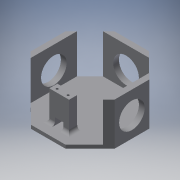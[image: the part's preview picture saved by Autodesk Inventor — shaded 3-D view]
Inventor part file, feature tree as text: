
AUTODESK INVENTOR PART (.ipt)
format: ipt  version: 2017 (Build 210142000, 142)  size: 202,752 bytes
history: native  units: in
note: dims shown in document units (in); Inventor stores cm internally (conversion verified against a paired STEP export)
features: reference x10, extrude x9, sketch x9, other x6, fillet x1
ambient origin geometry x8: Origin, YZ Plane, XZ Plane, XY Plane, X Axis, Y Axis, Z Axis, Center Point
bodies: Solid1 (feature_tree)
feature tree (35):
  extrude  "Extrusion1"  Depth=0.125in TaperAngle=0.0deg
  extrude  "Extrusion2"  Depth=0.205in
  extrude  "Extrusion3"  Depth=1.4in
  extrude  "Extrusion4"  Depth=0.01in
  extrude  "Extrusion5"  Depth=0.205in
  extrude  "Extrusion6"  Depth=1.4in
  extrude  "Extrusion7"  Depth=1.05in TaperAngle=0.0deg
  extrude  "Extrusion8"  Depth=0.08in
  extrude  "Extrusion9"  Depth=0.5in TaperAngle=0.0deg
  fillet  "Fillet2"  Radius=0.2045in
  sketch  "Sketch1"  dims[d0=3.0in d1=0.125in d2=0.0in]
  sketch  "Sketch3"  dims[d5=0.205in d6=0.205in]
  sketch  "Sketch5"  dims[d7=1.4in d8=0.0in d9=0.01in]
  reference  "Reference1"
  sketch  "Sketch6"  dims[d10=1.04in d11=0.0in d12=0.01in]
  reference  "Reference2"
  sketch  "Sketch7"  dims[d13=1.04in d14=0.0in d15=0.205in]
  sketch  "Sketch8"  dims[d16=1.4in d17=0.0in d18=0.01in]
  reference  "Reference3"
  sketch  "Sketch9"  dims[d19=1.04in d20=0.0in d21=1.05in d22=0.0in]
  reference  "Reference4"
  reference  "Reference5"
  reference  "Reference6"
  sketch  "Sketch10"  dims[d24=0.0531in d25=0.08in]
  reference  "Reference7"
  reference  "Reference8"
  reference  "Reference9"
  reference  "Reference10"
  sketch  "Sketch11"  dims[d26=0.08in d27=0.5in d28=0.0in d31=0.2045in d32=0.3in d33=0.25in d34=0.5in d35=0.0in d36=0.0in d37=0.125in]
  parser-record x1  (decoder bookkeeping rows leaked as tree rows — omitted from the tree; the rows remain in map.json)
  other  "Main_Assy.iam"
  other  "PIR_Sensor:1"
  other  "PIR_Sensor:3"
  other  "PIR_Sensor:2"
  other  "Servo Futaba S3003:1"
note: 1 file-system path scrubbed to <path> (originals preserved in map.json)
